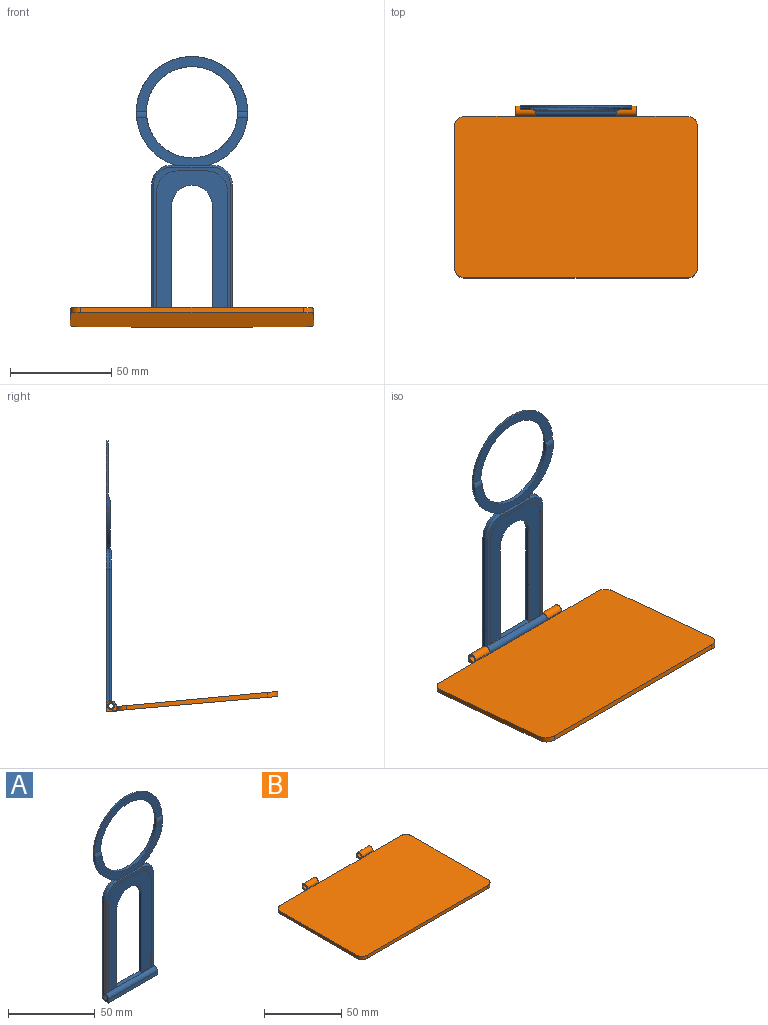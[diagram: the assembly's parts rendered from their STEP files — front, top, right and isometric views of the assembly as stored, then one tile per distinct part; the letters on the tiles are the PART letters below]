
ASSEMBLY  parts=2 mates=1
PART A: 35 faces, bbox 55x5.2x133.6 mm
  f0: plane 1.5x1.28mm, normal (0,0,1), area 1.9mm2, adj f4,f6,f8,f29
  f1: plane 54.77x23.71mm, normal (0,-1,0), area 353.3mm2, adj f5,f6,f14,f15,f29
  f2: plane 34.87x2.5mm, normal (0,0,1), area 57.4mm2, adj f3,f4,f16,f18,f19,f21,f25
  f3: plane 72.07x34.87mm, normal (0,-1,0), area 1213.4mm2, adj f2,f18,f19,f20,f21,f22,f23,f24
  f4: plane 132.58x55mm, normal (0,1,0), area 2628.8mm2, adj f0,f2,f5,f6,f7,f8,f9,f11
  f5: cylinder r=22.5mm len=45mm, axis (0,1,0), area 211.1mm2, adj f1,f4,f13,f14,f15
  f6: cylinder r=27.5mm len=55mm, axis (0,1,0), area 222.9mm2, adj f0,f1,f4,f7,f13,f14,f15,f29
  f7: plane 1.5x1.28mm, normal (0,0,1), area 1.9mm2, adj f4,f6,f12,f29
  f8: cylinder r=10mm len=10mm, axis (0,1,0), area 23.6mm2, adj f0,f4,f9,f30
  f9: plane 70x5.24mm, normal (-1,0,0), area 116mm2, adj f4,f8,f10,f16,f17,f31,f32,f33
  f10: plane 40x4.24mm, normal (0,0,-1), area 169.6mm2, adj f9,f11,f33,f34
  f11: plane 70x5.24mm, normal (1,0,0), area 116mm2, adj f4,f10,f12,f16,f17,f27,f32,f33
  f12: cylinder r=10mm len=10mm, axis (0,1,0), area 23.6mm2, adj f4,f7,f11,f28
  f13: plane 54.99x27mm, normal (0,-1,0), area 387.7mm2, adj f5,f6,f14,f15
  f14: cylinder r=5mm len=5.14mm, axis (1,0,0), area 16.1mm2, adj f1,f5,f6,f13
  f15: cylinder r=5mm len=5.14mm, axis (1,0,0), area 16.1mm2, adj f1,f5,f6,f13
  f16: cylinder r=2.5mm len=40mm, axis (1,0,0), area 157.5mm2, adj f2,f9,f11,f26,f27,f31,f32
  f17: cylinder r=1.25mm len=40mm, axis (1,0,0), area 314.2mm2, adj f9,f11
  f18: plane 55x2mm, normal (1,0,0), area 110mm2, adj f2,f3,f4,f20
  f19: plane 55x2mm, normal (-1,0,0), area 110mm2, adj f2,f3,f4,f20
  f20: cylinder r=10mm len=20mm, axis (0,-1,0), area 62.8mm2, adj f3,f4,f18,f19
  f21: plane 62.07x0.5mm, normal (1,0,0), area 31mm2, adj f2,f3,f22,f26
  f22: cylinder r=10mm len=10mm, axis (0,1,0), area 7.9mm2, adj f3,f21,f23,f26
  f23: plane 14.87x0.5mm, normal (0,0,-1), area 7.4mm2, adj f3,f22,f24,f26
  f24: cylinder r=10mm len=10mm, axis (0,1,0), area 7.9mm2, adj f3,f23,f25,f26
  f25: plane 62.07x0.5mm, normal (-1,0,0), area 31mm2, adj f2,f3,f24,f26
  f26: plane 74x38mm, normal (0,-1,0), area 306.7mm2, adj f16,f21,f22,f23,f24,f25,f27,f28
  f27: cylinder r=1mm len=65.21mm, axis (0,0,-1), area 102.2mm2, adj f11,f16,f26,f28
  f28: torus R=9mm, axis (0,-1,0), area 23.8mm2, adj f12,f26,f27,f29
  f29: cylinder r=1mm len=20mm, axis (1,0,0), area 22.4mm2, adj f0,f1,f6,f7,f26,f28,f30
  f30: torus R=9mm, axis (0,-1,0), area 23.8mm2, adj f8,f26,f29,f31
  f31: cylinder r=1mm len=65.21mm, axis (0,0,1), area 102.2mm2, adj f9,f16,f26,f30
  f32: plane 40x0.02mm, normal (0,0,1), area 0.8mm2, adj f9,f11,f16,f33
  f33: plane 40x2.5mm, normal (0,-1,0.09), area 100.4mm2, adj f9,f10,f11,f32
  f34: plane 40x1mm, normal (0,0.71,-0.71), area 56.6mm2, adj f4,f9,f10,f11
PART B: 24 faces, bbox 120x85x5 mm
  f0: plane 40x2mm, normal (0,1,0), area 80mm2, adj f5,f11,f12,f19
  f1: plane 25x2mm, normal (0,1,0), area 50mm2, adj f7,f12,f19,f20
  f2: plane 70x2.47mm, normal (-1,0,0), area 157.5mm2, adj f12,f19,f20,f21
  f3: plane 70x2.47mm, normal (1,0,0), area 157.5mm2, adj f12,f19,f22,f23
  f4: plane 25x2mm, normal (0,1,0), area 50mm2, adj f9,f12,f19,f23
  f5: plane 5x5mm, normal (1,0,0), area 12.7mm2, adj f0,f6,f12,f14,f15,f18
  f6: plane 10x2.5mm, normal (0,1,0), area 25mm2, adj f5,f7,f12,f15
  f7: plane 5x5mm, normal (-1,0,0), area 12.7mm2, adj f1,f6,f12,f14,f15,f18
  f8: plane 110x2.5mm, normal (0,-1,0), area 275mm2, adj f12,f19,f21,f22
  f9: plane 5x5mm, normal (1,0,0), area 12.7mm2, adj f4,f10,f12,f13,f16,f17
  f10: plane 10x2.5mm, normal (0,1,0), area 25mm2, adj f9,f11,f12,f16
  f11: plane 5x5mm, normal (-1,0,0), area 12.7mm2, adj f0,f10,f12,f13,f16,f17
  f12: plane 120x85mm, normal (0,0,-1), area 9678.5mm2, adj f0,f1,f2,f3,f4,f5,f6,f7
  f13: cylinder r=1.75mm len=10mm, axis (-1,0,0), area 110mm2, adj f9,f11
  f14: cylinder r=1.75mm len=10mm, axis (-1,0,0), area 110mm2, adj f5,f7
  f15: cylinder r=2.5mm len=10mm, axis (1,0,0), area 78.5mm2, adj f5,f6,f7,f18
  f16: cylinder r=2.5mm len=10mm, axis (1,0,0), area 78.5mm2, adj f9,f10,f11,f17
  f17: plane 10x0.5mm, normal (0,-1,0), area 5mm2, adj f9,f11,f16,f19
  f18: plane 10x0.5mm, normal (0,-1,0), area 5mm2, adj f5,f7,f15,f19
  f19: plane 120.01x80.01mm, normal (0,0.01,1), area 9578.7mm2, adj f0,f1,f2,f3,f4,f8,f17,f18
  f20: cylinder r=5mm len=5mm, axis (0,0,1), area 15.8mm2, adj f1,f2,f12,f19
  f21: cylinder r=5mm len=5mm, axis (0,0,-1), area 19.5mm2, adj f2,f8,f12,f19
  f22: cylinder r=5mm len=5mm, axis (0,0,1), area 19.5mm2, adj f3,f8,f12,f19
  f23: cylinder r=5mm len=5mm, axis (0,0,-1), area 15.8mm2, adj f3,f4,f12,f19
PLACE A t=(-8.39,41.12,55.96)mm fixed
PLACE B rot(axis=(-1,0,0),5deg) t=(-8.39,-3.94,23.41)mm
MATE revolute A.f16 <-> B.f16  axis (1,0,0) through (11.61,38.62,22.19)mm
